# Revit family: 402_1a984f0283b94affac206fece93ad0
name_source: partatom
category: Mechanical Equipment
revit_build: Autodesk Revit 2018 (Build: 20170223_1515(x64)
units: mm (PartAtom-declared; Revit-internal decimal feet)

## family parameters
Always vertical = Yes
Cut with Voids When Loaded = No
Part Type = Normal
Room Calculation Point = No
Round Connector Dimension = Use Diameter
Shared = No
Work Plane-Based = No

## types (1)
- VCIN1A200-P2 vertical
    CAT0 = 1 mm  [stored 0.00328084 ft]
    DP = 500 mm  [stored 1.64042 ft]
    Description = Air curtain INDESSE, length 2,2m, water coil (warm water 110°C), antifreeze protection
    H1 = 194 mm  [stored 0.636483 ft]
    H2 = 200 mm
    H3 = 40 mm  [stored 0.131234 ft]
    HP = 117 mm  [stored 0.383858 ft]
    HP__ve = -117 mm  [stored -0.383858 ft]
    L = 2200 mm  [stored 7.21785 ft]
    L__ve = -2200 mm  [stored -7.21785 ft]
    MC Product Code = VCIN1A200-P2 vertical
    Manufacturer = 2VV
    PD = 825 mm  [stored 2.70669 ft]
    QmdConnectorList = 331;PHS;361;PHR
    URL = www.2vv.cz
    W2 = 252 mm  [stored 0.826772 ft]
    W22 = 126 mm  [stored 0.413386 ft]
    XP = 276 mm
    YP = 1038 mm  [stored 3.40551 ft]
    ZL = 1100 mm  [stored 3.60892 ft]
    ZP = 127 mm  [stored 0.416667 ft]
    ZPD = 275 mm  [stored 0.902231 ft]
    magiPartTypeId = 402
    magiProductFamilyId = 1a984f0283b94affac206fece93ad0
    magiProductId = 0ea58ff2603c4bbc9467c79e83ba09

note: [stored X ft] marks values corroborated as IEEE doubles in the binary element streams (Revit-internal decimal feet)

## geometry (parser evidence)
native form markers: Blend x2, Sweep x3
no freeform markers — native parametric forms only
